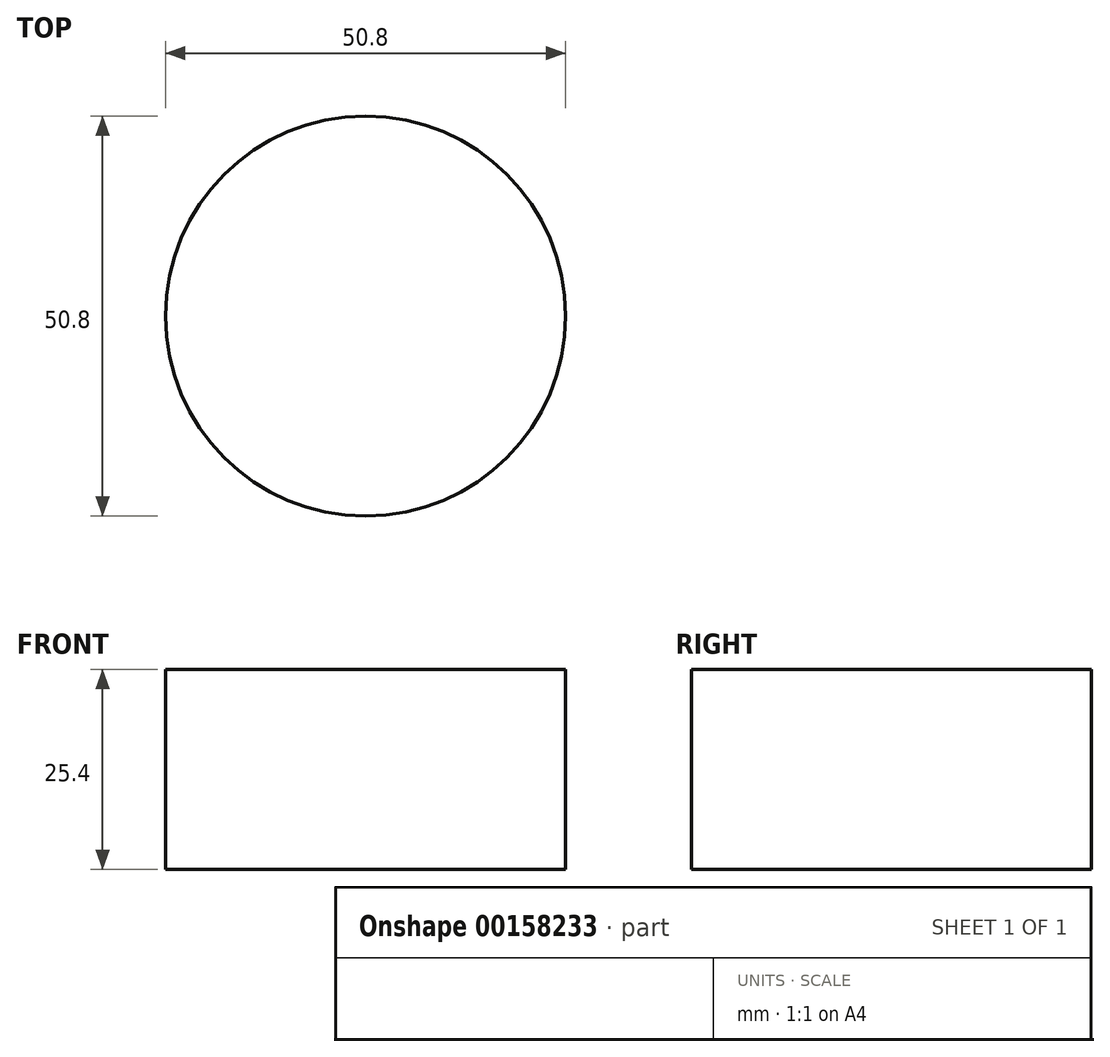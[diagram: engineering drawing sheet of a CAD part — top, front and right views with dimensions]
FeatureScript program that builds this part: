
annotation { "Feature Type Name" : "Feature", "Feature Type Description" : "" }
export const myFeature = defineFeature(function(context is Context, id is Id, definition is map)
    precondition{}
    {
        {
            var Q0;
            Q0=qCreatedBy(makeId("Top.planeOp"),FACE);
            var sketch = newSketch(context, id + "F0", { "sketchPlane" : qUnion([Q0])});
            skCircle(sketch, "E0", {"center": v(0, 0) * mm, "radius": 25.4 * mm});
            skSolve(sketch);
        }
        {
            var Q0;
            Q0 = qSketchRegion(id + "F0", true);
            extrude(context, id + "F1", {"entities" : qUnion([Q0]), "endBound" : BoundingType.SYMMETRIC, "depth" : 25.4 * mm});
        }
    });
